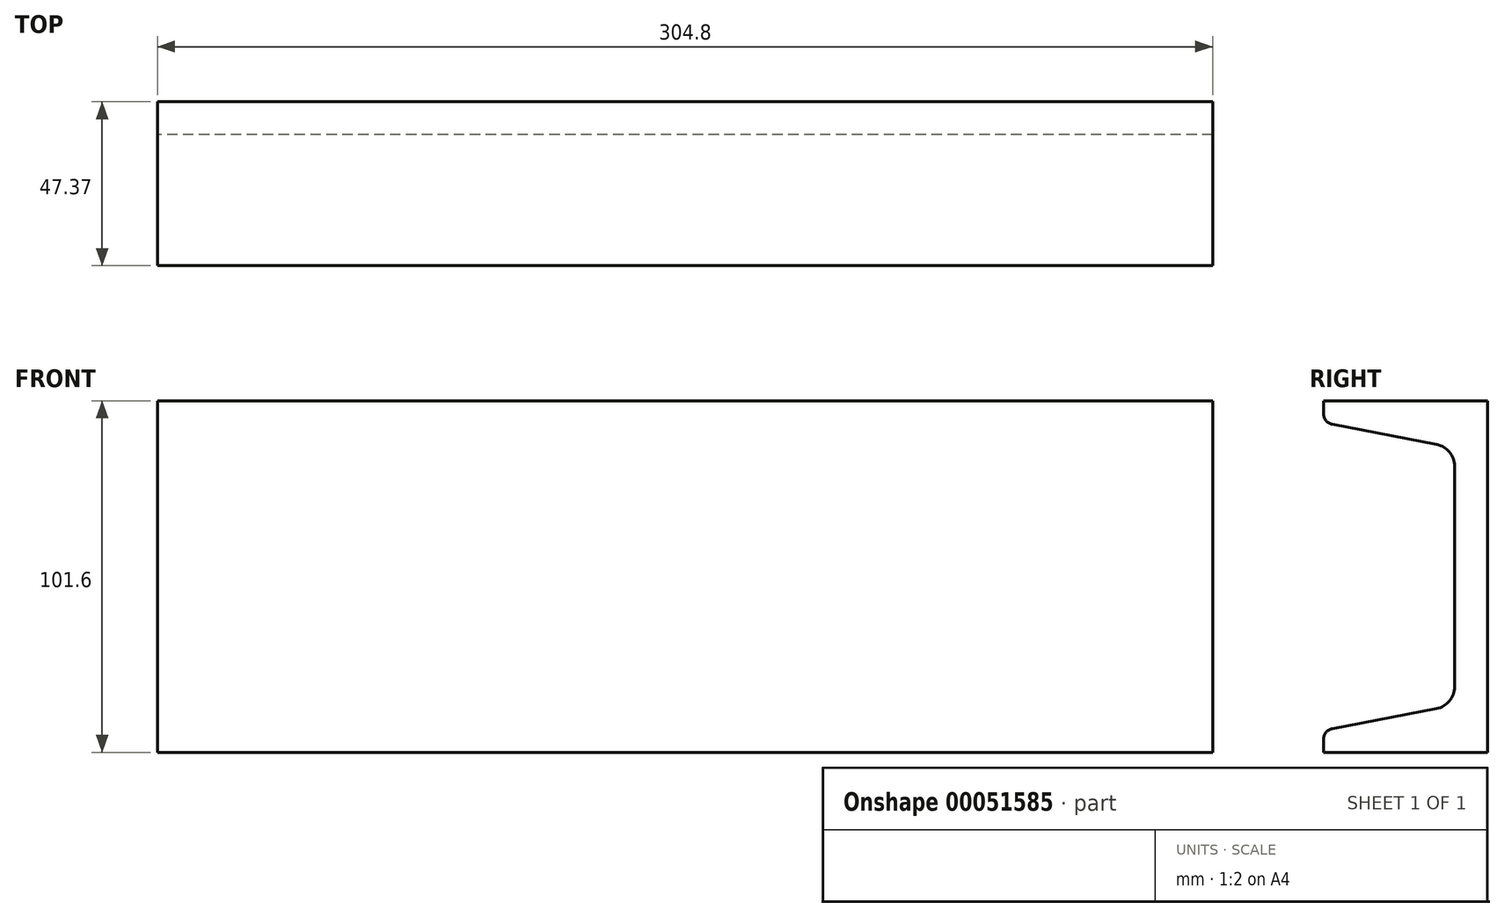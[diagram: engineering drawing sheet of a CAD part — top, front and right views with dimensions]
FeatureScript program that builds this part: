
annotation { "Feature Type Name" : "Feature", "Feature Type Description" : "" }
export const myFeature = defineFeature(function(context is Context, id is Id, definition is map)
    precondition{}
    {
        {
            var Q0;
            Q0=qCreatedBy(makeId("Right.planeOp"),FACE);
            var sketch = newSketch(context, id + "F0", { "sketchPlane" : qUnion([Q0])});
            skLineSegment(sketch, "E0", {"start": v(0, 50.8) * mm, "end": v(0, 0) * mm});
            skLineSegment(sketch, "E1", {"start": v(0, 50.8) * mm, "end": v(-47.37, 50.8) * mm});
            skLineSegment(sketch, "E2", {"start": v(-47.37, 50.8) * mm, "end": v(-47.37, 47.07) * mm});
            skLineSegment(sketch, "E3", {"start": v(-44.8, 43.95) * mm, "end": v(-14.67, 38.15) * mm});
            skLineSegment(sketch, "E4", {"start": v(-9.53, 31.92) * mm, "end": v(-9.52, 0) * mm});
            skPoint(sketch, "E5.visualSharp", {"position": v(-9.53, 37.16) * mm});
            skArc(sketch, "E5.filletArc", {"start": v(-9.52, 31.92) * mm, "mid": v(-10.98, 35.96) * mm, "end": v(-14.67, 38.15) * mm});
            skPoint(sketch, "E6.visualSharp", {"position": v(-47.37, 44.45) * mm});
            skArc(sketch, "E6.filletArc", {"start": v(-47.37, 47.07) * mm, "mid": v(-46.64, 45.05) * mm, "end": v(-44.8, 43.95) * mm});
            skLineSegment(sketch, "E7", {"start": v(68.21, 0) * mm, "end": v(-68.93, 0) * mm, "construction": true});
            skLineSegment(sketch, "E8.MirrorCS", {"start": v(0, -50.8) * mm, "end": v(0, 0) * mm});
            skLineSegment(sketch, "E9.MirrorCS", {"start": v(0, -50.8) * mm, "end": v(-47.37, -50.8) * mm});
            skLineSegment(sketch, "E10.MirrorCS", {"start": v(-9.53, -31.92) * mm, "end": v(-9.52, 0) * mm});
            skArc(sketch, "E11.MirrorCS", {"start": v(-9.52, -31.92) * mm, "mid": v(-10.98, -35.96) * mm, "end": v(-14.67, -38.15) * mm});
            skLineSegment(sketch, "E12.MirrorCS", {"start": v(-44.8, -43.95) * mm, "end": v(-14.67, -38.15) * mm});
            skLineSegment(sketch, "E13.MirrorCS", {"start": v(-47.37, -50.8) * mm, "end": v(-47.37, -47.07) * mm});
            skArc(sketch, "E14.MirrorCS", {"start": v(-47.37, -47.07) * mm, "mid": v(-46.64, -45.05) * mm, "end": v(-44.8, -43.95) * mm});
            skSolve(sketch);
        }
        {
            var Q0;
            Q0=makeQuery(id+"F0.imprint","IMPRINT",FACE,{"disambiguationData":[TD([[makeQuery(id+"F0.imprint","IMPRINT",EDGE,{"derivedFrom":sQuery(id+"F0.wireOp",EDGE,"E0")}),-1.0]])]});
            extrude(context, id + "F1", {"entities" : qUnion([Q0]), "depth" : 304.8 * mm});
        }
    });
